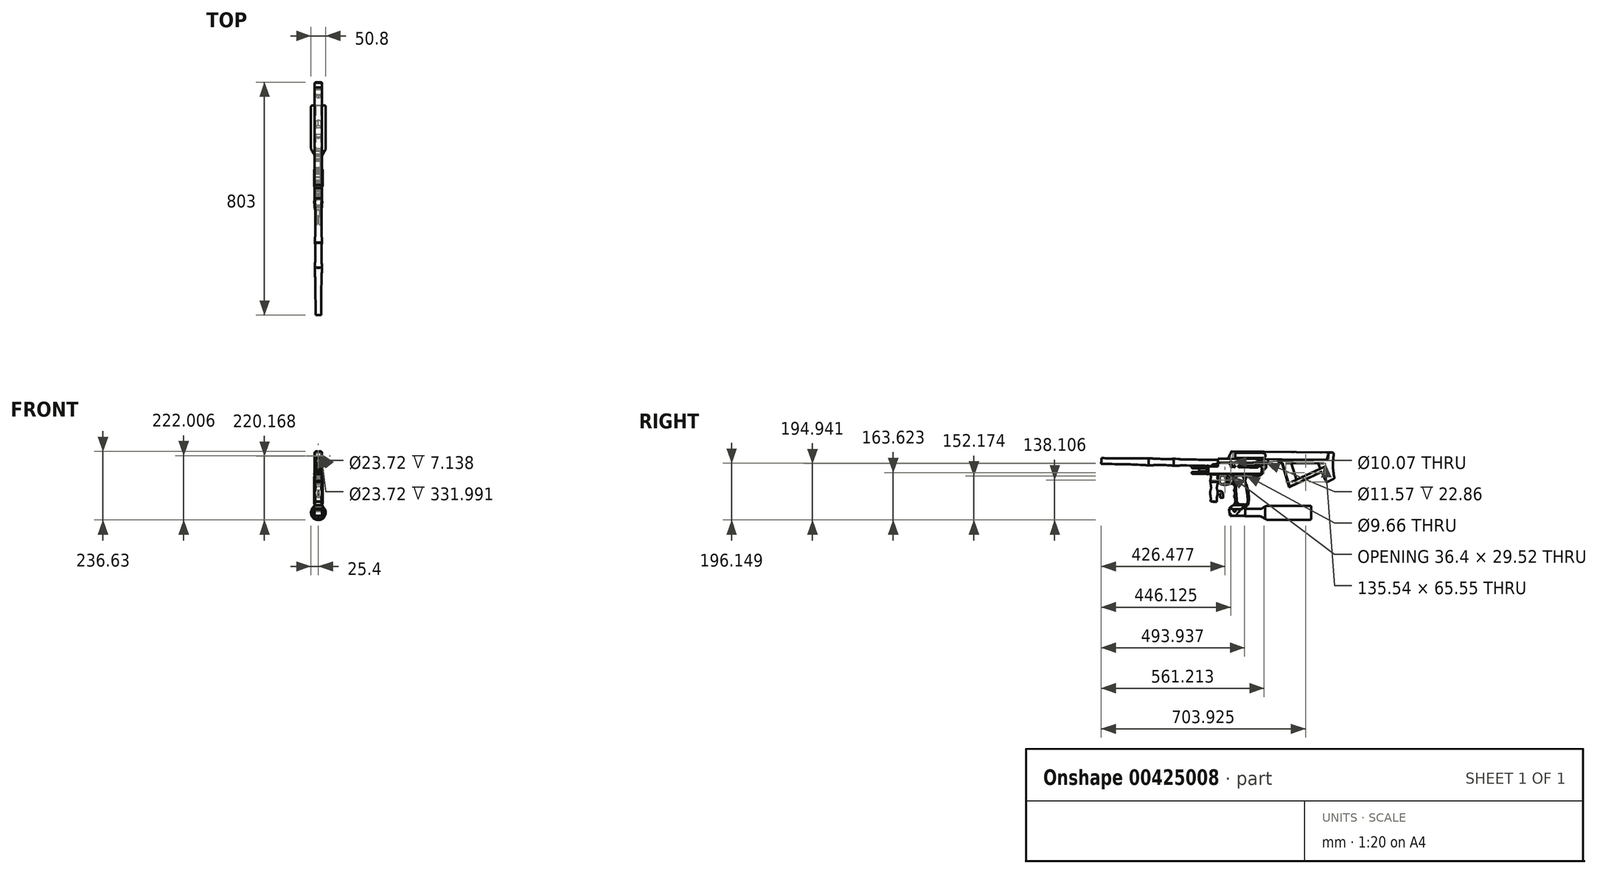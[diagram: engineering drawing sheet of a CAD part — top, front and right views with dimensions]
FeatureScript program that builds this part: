
annotation { "Feature Type Name" : "Feature", "Feature Type Description" : "" }
export const myFeature = defineFeature(function(context is Context, id is Id, definition is map)
    precondition{}
    {
        {
            var Q0;
            Q0=qCreatedBy(makeId("Right.planeOp"),FACE);
            var sketch = newSketch(context, id + "F0", { "sketchPlane" : qUnion([Q0])});
            skLineSegment(sketch, "E0", {"start": v(0, 12.7) * mm, "end": v(55.88, 12.7) * mm});
            skLineSegment(sketch, "E1", {"start": v(55.88, 12.7) * mm, "end": v(76.2, 25.4) * mm});
            skLineSegment(sketch, "E2", {"start": v(76.2, 25.4) * mm, "end": v(228.6, 25.4) * mm});
            skLineSegment(sketch, "E3", {"start": v(228.6, 25.4) * mm, "end": v(228.6, 0) * mm});
            skLineSegment(sketch, "E4", {"start": v(0, 12.7) * mm, "end": v(0, 0) * mm});
            skLineSegment(sketch, "E5", {"start": v(0, 0) * mm, "end": v(228.6, 0) * mm});
            skLineSegment(sketch, "E6", {"start": v(38.1, 12.7) * mm, "end": v(38.1, 0) * mm, "construction": true});
            skSolve(sketch);
        }
        {
            var Q0;
            Q0=makeQuery(id+"F0.imprint","IMPRINT",FACE,{"disambiguationData":[TD([[makeQuery(id+"F0.imprint","IMPRINT",EDGE,{"derivedFrom":sQuery(id+"F0.wireOp",EDGE,"E0")}),-1.0]])]});
            var Q1;
            Q1=sQuery(id+"F0.wireOp",EDGE,"E5");
            revolve(context, id + "F1", {"entities" : qUnion([Q0]), "axis" : qUnion([Q1]), "revolveType" : RevolveType.FULL});
        }
        {
            var Q0;
            Q0=makeQuery(id+"F1.opRevolve","SWEPT_EDGE",EDGE,{"disambiguationData":[OSD([sQuery(id+"F0.wireOp",EDGE,"E0"),sQuery(id+"F0.wireOp",EDGE,"E1")])]});
            fillet(context, id + "F2", {"entities" : qUnion([Q0]), "radius" : 12.7 * mm, "tangentPropagation" : true, "allowEdgeOverflow" : false});
        }
        {
            var Q0;
            Q0=makeQuery(id+"F1.opRevolve","SWEPT_EDGE",EDGE,{"disambiguationData":[OSD([sQuery(id+"F0.wireOp",EDGE,"E1"),sQuery(id+"F0.wireOp",EDGE,"E2")])]});
            fillet(context, id + "F3", {"entities" : qUnion([Q0]), "radius" : 25.4 * mm, "tangentPropagation" : true, "allowEdgeOverflow" : false});
        }
        {
            var Q0;
            Q0=makeQuery(id+"F1.opRevolve","SWEPT_EDGE",EDGE,{"disambiguationData":[OSD([sQuery(id+"F0.wireOp",EDGE,"E2"),sQuery(id+"F0.wireOp",EDGE,"E3")])]});
            fillet(context, id + "F4", {"entities" : qUnion([Q0]), "radius" : 5.08 * mm, "tangentPropagation" : true, "allowEdgeOverflow" : false});
        }
        {
            var Q0;
            Q0=qCreatedBy(makeId("Right.planeOp"),FACE);
            var sketch = newSketch(context, id + "F5", { "sketchPlane" : qUnion([Q0])});
            skLineSegment(sketch, "E7", {"start": v(-34.8, 25.58) * mm, "end": v(8.85, 25.58) * mm});
            skArc(sketch, "E8", {"start": v(8.85, 25.58) * mm, "mid": v(11.47, 26.54) * mm, "end": v(12.84, 28.97) * mm});
            skArc(sketch, "E9", {"start": v(12.84, 28.97) * mm, "mid": v(13.6, 66.51) * mm, "end": v(3.93, 102.8) * mm});
            skArc(sketch, "E10", {"start": v(20.6, 127.96) * mm, "mid": v(5.51, 119.85) * mm, "end": v(3.93, 102.8) * mm});
            skLineSegment(sketch, "E11", {"start": v(20.6, 127.96) * mm, "end": v(51.69, 127.96) * mm});
            skLineSegment(sketch, "E12", {"start": v(36.38, 133.85) * mm, "end": v(57.22, 133.85) * mm});
            skLineSegment(sketch, "E13", {"start": v(57.22, 133.85) * mm, "end": v(57.22, 130.34) * mm});
            skLineSegment(sketch, "E14", {"start": v(57.22, 130.34) * mm, "end": v(51.69, 127.96) * mm});
            skLineSegment(sketch, "E15", {"start": v(36.38, 133.85) * mm, "end": v(-87.79, 133.99) * mm});
            skLineSegment(sketch, "E16", {"start": v(-87.79, 133.99) * mm, "end": v(-87.82, 103.6) * mm});
            skArc(sketch, "E17", {"start": v(-87.82, 103.6) * mm, "mid": v(-86.98, 100.92) * mm, "end": v(-84.74, 99.2) * mm});
            skArc(sketch, "E18", {"start": v(-84.74, 99.2) * mm, "mid": v(-67.88, 96.22) * mm, "end": v(-51.03, 99.2) * mm});
            skArc(sketch, "E19", {"start": v(-35.1, 80.6) * mm, "mid": v(-36.61, 95.42) * mm, "end": v(-51.03, 99.2) * mm});
            skLineSegment(sketch, "E20", {"start": v(36.38, 133.85) * mm, "end": v(36.38, 127.96) * mm});
            skLineSegment(sketch, "E21", {"start": v(-35.1, 80.6) * mm, "end": v(-37.34, 76.5) * mm});
            skArc(sketch, "E22", {"start": v(-37.34, 55.45) * mm, "mid": v(-33.29, 65.98) * mm, "end": v(-37.34, 76.5) * mm});
            skArc(sketch, "E23", {"start": v(-34.39, 32.06) * mm, "mid": v(-31.83, 44.26) * mm, "end": v(-37.34, 55.45) * mm});
            skArc(sketch, "E24", {"start": v(-34.39, 32.06) * mm, "mid": v(-35.38, 28.87) * mm, "end": v(-34.8, 25.58) * mm});
            skFitSpline(sketch, "E25", {"points": [v(-85.65, 112.62) * mm, v(-85.36, 121.7) * mm, v(-85, 123.52) * mm, v(-84.11, 124.91) * mm, v(-82.58, 126.23) * mm, v(-80.53, 127.18) * mm, v(-62.02, 127.4) * mm, v(-58.15, 126.45) * mm, v(-54.42, 124.76) * mm, v(-51.56, 121.91) * mm, v(-49.59, 117.45) * mm, v(-49.22, 112.55) * mm, v(-50.17, 106.4) * mm, v(-52.15, 102.6) * mm, v(-55.59, 99.97) * mm, v(-59.83, 98.43) * mm, v(-70.87, 98.07) * mm, v(-81.63, 99.9) * mm, v(-84.7, 102.16) * mm, v(-85.72, 105.23) * mm, v(-85.65, 112.62) * mm]});
            skArc(sketch, "E26", {"start": v(-26.53, 127.42) * mm, "mid": v(-29.86, 126.09) * mm, "end": v(-31.18, 122.76) * mm});
            skArc(sketch, "E27", {"start": v(-4.85, 122.48) * mm, "mid": v(-7.37, 125.75) * mm, "end": v(-11.28, 127.05) * mm});
            skArc(sketch, "E28", {"start": v(10.82, 32.35) * mm, "mid": v(7.26, 78.16) * mm, "end": v(-4.85, 122.48) * mm});
            skArc(sketch, "E29", {"start": v(5.99, 27.7) * mm, "mid": v(9.37, 29.02) * mm, "end": v(10.82, 32.35) * mm});
            skArc(sketch, "E30", {"start": v(-26.4, 32.85) * mm, "mid": v(-24.9, 29.7) * mm, "end": v(-21.66, 28.36) * mm});
            skArc(sketch, "E31", {"start": v(-31.18, 122.76) * mm, "mid": v(-29.39, 77.77) * mm, "end": v(-26.4, 32.85) * mm});
            skLineSegment(sketch, "E32", {"start": v(-26.53, 127.42) * mm, "end": v(-11.28, 127.05) * mm});
            skLineSegment(sketch, "E33", {"start": v(-21.66, 28.36) * mm, "end": v(5.99, 27.7) * mm});
            skFitSpline(sketch, "E34", {"points": [v(-42.23, 99.25) * mm, v(-39.9, 104.21) * mm, v(-38.86, 113.42) * mm, v(-40.72, 121.38) * mm, v(-45.27, 128.83) * mm, v(-50.65, 133.95) * mm], "startDerivative": vector(15.33, 26.3) * mm, "endDerivative": vector(-28.38, 23.96) * mm});
            skLineSegment(sketch, "E35", {"start": v(-50.31, 105.95) * mm, "end": v(-59.35, 105.95) * mm});
            skLineSegment(sketch, "E36", {"start": v(-62.76, 127.47) * mm, "end": v(-63.34, 125.85) * mm});
            skLineSegment(sketch, "E37", {"start": v(-63.34, 125.85) * mm, "end": v(-66.8, 123.46) * mm});
            skLineSegment(sketch, "E38", {"start": v(-66.8, 123.46) * mm, "end": v(-66.8, 121.65) * mm});
            skArc(sketch, "E39", {"start": v(-59.35, 105.95) * mm, "mid": v(-59, 116.44) * mm, "end": v(-66.8, 123.46) * mm});
            skArc(sketch, "E40", {"start": v(-68.63, 101.75) * mm, "mid": v(-64.25, 110.54) * mm, "end": v(-68.14, 119.55) * mm});
            skArc(sketch, "E41", {"start": v(-68.63, 101.75) * mm, "mid": v(-68.81, 100.98) * mm, "end": v(-68.11, 100.6) * mm});
            skArc(sketch, "E42", {"start": v(-68.11, 100.6) * mm, "mid": v(-63.21, 102.43) * mm, "end": v(-59.35, 105.95) * mm});
            skLineSegment(sketch, "E43", {"start": v(-68.14, 119.55) * mm, "end": v(-66.8, 121.65) * mm});
            skLineSegment(sketch, "E44", {"start": v(-119.06, 133.99) * mm, "end": v(-90.1, 133.99) * mm});
            skLineSegment(sketch, "E45", {"start": v(-116.98, 37.9) * mm, "end": v(-95.76, 37.9) * mm});
            skLineSegment(sketch, "E46", {"start": v(-104.57, 133.99) * mm, "end": v(-106.37, 37.9) * mm});
            skFitSpline(sketch, "E47", {"points": [v(-95.76, 37.9) * mm, v(-95.76, 41) * mm, v(-95.76, 50.82) * mm, v(-94.35, 58.22) * mm, v(-93.32, 64.11) * mm, v(-93.53, 75.08) * mm, v(-94.77, 80.46) * mm, v(-95.76, 85.73) * mm, v(-94.54, 92.26) * mm, v(-93.18, 100.75) * mm, v(-92.32, 106.04) * mm, v(-92.07, 109.62) * mm, v(-92.32, 114.77) * mm, v(-93.8, 119.44) * mm, v(-93.43, 123.75) * mm, v(-92.2, 129.29) * mm, v(-90.1, 133.99) * mm], "startDerivative": vector(1.1, 57.96) * mm, "endDerivative": vector(36.56, 91.45) * mm});
            skLineSegment(sketch, "E48", {"start": v(-105.1, 105.63) * mm, "end": v(-92.41, 105.4) * mm});
            skLineSegment(sketch, "E49", {"start": v(-105.03, 109.62) * mm, "end": v(-92.07, 109.62) * mm});
            skLineSegment(sketch, "E50", {"start": v(-90.1, 133.99) * mm, "end": v(-87.79, 133.99) * mm});
            skLineSegment(sketch, "E51", {"start": v(-87.79, 133.99) * mm, "end": v(-87.79, 133.99) * mm});
            skLineSegment(sketch, "E52", {"start": v(-119.06, 133.99) * mm, "end": v(-119.88, 136.58) * mm, "construction": true});
            skLineSegment(sketch, "E53", {"start": v(-119.88, 136.58) * mm, "end": v(-124.7, 136.58) * mm, "construction": true});
            skLineSegment(sketch, "E54", {"start": v(-124.7, 136.58) * mm, "end": v(-124.7, 159) * mm});
            skLineSegment(sketch, "E55", {"start": v(-124.7, 159) * mm, "end": v(-91.58, 159) * mm});
            skLineSegment(sketch, "E56", {"start": v(-91.58, 159) * mm, "end": v(-91.58, 186.35) * mm});
            skLineSegment(sketch, "E57", {"start": v(-91.58, 186.35) * mm, "end": v(58.12, 184.65) * mm});
            skLineSegment(sketch, "E58", {"start": v(58.12, 184.65) * mm, "end": v(80.35, 183.9) * mm});
            skFitSpline(sketch, "E59", {"points": [v(80.35, 183.9) * mm, v(80.35, 175.9) * mm, v(79.82, 173.8) * mm, v(77.49, 172.2) * mm, v(76.32, 170.65) * mm, v(74.97, 167.4) * mm, v(74.47, 162.84) * mm, v(74.1, 156.94) * mm, v(72.88, 153.08) * mm, v(70.84, 151.59) * mm, v(66.54, 147.1) * mm, v(62.97, 139.71) * mm, v(61.31, 134.42) * mm, v(61.08, 133.83) * mm, v(60.68, 133.46) * mm, v(57.22, 133.33) * mm], "startDerivative": vector(0.59, -95.8) * mm, "endDerivative": vector(-85.27, 1.37) * mm});
            skFitSpline(sketch, "E60", {"points": [v(58.12, 184.65) * mm, v(58.12, 180.63) * mm, v(57.78, 178.99) * mm, v(56.76, 178.55) * mm, v(42.34, 175.33) * mm, v(39.81, 174.2) * mm, v(39.03, 173.58) * mm, v(38.25, 172.1) * mm, v(37.88, 168.45) * mm, v(38.25, 166.07) * mm, v(39.97, 164.06) * mm, v(44.25, 162.64) * mm, v(50.45, 161.47) * mm, v(55.52, 159.55) * mm, v(58.12, 157.64) * mm, v(58.98, 156.2) * mm, v(58.37, 133.3) * mm], "startDerivative": vector(0, -170.26) * mm, "endDerivative": vector(-0.04, -213.8) * mm});
            skFitSpline(sketch, "E61", {"points": [v(59.43, 176.27) * mm, v(46.5, 174.05) * mm, v(43.35, 173.42) * mm, v(41.9, 172.4) * mm, v(40.6, 170.58) * mm, v(40.6, 168.87) * mm, v(41.02, 167.01) * mm, v(42.37, 166.03) * mm, v(51.37, 163.75) * mm, v(55.97, 162.46) * mm, v(59.95, 162.51) * mm, v(60.68, 163.8) * mm, v(61.2, 165.61) * mm, v(59.8, 167.94) * mm, v(59.43, 170.22) * mm, v(60.16, 171.98) * mm, v(60.83, 173.73) * mm, v(60.57, 175.34) * mm, v(59.43, 176.27) * mm]});
            skCircle(sketch, "E62", {"center": v(67.35, 169.54) * mm, "radius": 5.78 * mm});
            skCircle(sketch, "E63", {"center": v(0.08, 126.77) * mm, "radius": 4.83 * mm});
            skCircle(sketch, "E64", {"center": v(-47.74, 170.75) * mm, "radius": 5.03 * mm});
            skLineSegment(sketch, "E65", {"start": v(-91.58, 182.73) * mm, "end": v(-91.58, 159.18) * mm});
            skLineSegment(sketch, "E66", {"start": v(-493.5, 187.98) * mm, "end": v(-493.5, 168.75) * mm});
            skLineSegment(sketch, "E67", {"start": v(-493.5, 178.36) * mm, "end": v(-91.58, 170.96) * mm});
            skFitSpline(sketch, "E68", {"points": [v(-91.58, 182.73) * mm, v(-119.26, 182.73) * mm, v(-132.58, 182.45) * mm, v(-141.54, 182.4) * mm, v(-218.62, 183.74) * mm, v(-221.32, 183.89) * mm, v(-223.33, 184.44) * mm, v(-225.09, 184.99) * mm, v(-228.56, 185.2) * mm, v(-244.1, 185.57) * mm, v(-247.38, 185.61) * mm, v(-248.94, 185.26) * mm, v(-250.38, 184.74) * mm, v(-253.38, 184.48) * mm, v(-258.12, 184.52) * mm, v(-306.46, 185.9) * mm, v(-318.87, 186.83) * mm, v(-329.63, 187.14) * mm, v(-343.7, 187.27) * mm, v(-381.34, 186.78) * mm, v(-423.66, 187.15) * mm, v(-493.5, 187.98) * mm], "startDerivative": vector(-460.1, 2.23) * mm, "endDerivative": vector(-701.67, 7.48) * mm});
            skLineSegment(sketch, "E69", {"start": v(-330.43, 175.36) * mm, "end": v(-330.21, 187.15) * mm});
            skLineSegment(sketch, "E70", {"start": v(-244.33, 173.77) * mm, "end": v(-244.1, 185.57) * mm});
            skFitSpline(sketch, "E71", {"points": [v(4.95, 25.58) * mm, v(5.8, 23.6) * mm, v(5.17, 21.07) * mm, v(3.34, 19.04) * mm, v(1.12, 19.26) * mm, v(-6.59, 18.86) * mm, v(-8.65, 17.1) * mm, v(-8.31, 15.51) * mm, v(-8.57, 12.67) * mm, v(-8.87, 12.04) * mm, v(-51.36, 12.84) * mm, v(-51.75, 12.98) * mm, v(-51.8, 17.75) * mm, v(-51.48, 18.04) * mm, v(-42.1, 23.94) * mm, v(-40.14, 25.32) * mm, v(-34.8, 25.58) * mm], "startDerivative": vector(22.9, -41.19) * mm, "endDerivative": vector(123.88, 5.53) * mm});
            skLineSegment(sketch, "E72", {"start": v(-49.82, 12.84) * mm, "end": v(-54.66, 10.86) * mm});
            skLineSegment(sketch, "E73", {"start": v(-54.66, 10.86) * mm, "end": v(-50.05, -10.71) * mm});
            skLineSegment(sketch, "E74", {"start": v(-50.05, -10.71) * mm, "end": v(1.1, -10.71) * mm});
            skLineSegment(sketch, "E75", {"start": v(1.1, -10.71) * mm, "end": v(1.1, 15.65) * mm});
            skLineSegment(sketch, "E76", {"start": v(1.1, 15.65) * mm, "end": v(-8.31, 15.51) * mm});
            skFitSpline(sketch, "E77", {"points": [v(-29.52, -10.71) * mm, v(-28.92, -8.02) * mm, v(-27.7, -5.93) * mm, v(-24.57, -1.75) * mm, v(-21.09, 1.81) * mm, v(-18.48, 4.86) * mm, v(-18.13, 7.12) * mm, v(-18.83, 9.56) * mm, v(-21.43, 11.86) * mm], "startDerivative": vector(4.19, 25.46) * mm, "endDerivative": vector(-24.07, 17.07) * mm});
            skCircle(sketch, "E78", {"center": v(-34.92, 7.3) * mm, "radius": 3.9 * mm});
            skLineSegment(sketch, "E79", {"start": v(-44.21, 159.76) * mm, "end": v(-35.63, 159.76) * mm});
            skLineSegment(sketch, "E80", {"start": v(-18.9, 159.55) * mm, "end": v(43.85, 158.68) * mm});
            skArc(sketch, "E81.0.startCap", {"start": v(-44.21, 158.5) * mm, "mid": v(-45.48, 159.76) * mm, "end": v(-44.21, 161.03) * mm});
            skArc(sketch, "E81.0.endCap", {"start": v(-35.63, 161.03) * mm, "mid": v(-34.36, 159.76) * mm, "end": v(-35.63, 158.5) * mm});
            skLineSegment(sketch, "E81.0.left", {"start": v(-44.21, 161.03) * mm, "end": v(-35.63, 161.03) * mm});
            skLineSegment(sketch, "E81.0.right", {"start": v(-44.21, 158.5) * mm, "end": v(-35.63, 158.5) * mm});
            skArc(sketch, "E81.1.startCap", {"start": v(-18.93, 158.28) * mm, "mid": v(-20.18, 159.57) * mm, "end": v(-18.9, 160.82) * mm});
            skArc(sketch, "E81.1.endCap", {"start": v(43.87, 159.95) * mm, "mid": v(45.12, 158.66) * mm, "end": v(43.83, 157.4) * mm});
            skLineSegment(sketch, "E81.1.left", {"start": v(-18.9, 160.82) * mm, "end": v(43.87, 159.95) * mm});
            skLineSegment(sketch, "E81.1.right", {"start": v(-18.93, 158.28) * mm, "end": v(43.83, 157.4) * mm});
            skLineSegment(sketch, "E82", {"start": v(-124.7, 159) * mm, "end": v(-124.7, 162.28) * mm});
            skLineSegment(sketch, "E83", {"start": v(-124.7, 162.28) * mm, "end": v(-130.05, 162.28) * mm});
            skLineSegment(sketch, "E84", {"start": v(-130.05, 162.28) * mm, "end": v(-130.05, 132.7) * mm});
            skLineSegment(sketch, "E85", {"start": v(-130.05, 132.7) * mm, "end": v(-124.7, 132.7) * mm});
            skLineSegment(sketch, "E86", {"start": v(-124.7, 132.7) * mm, "end": v(-124.7, 136.58) * mm});
            skLineSegment(sketch, "E87", {"start": v(-130.05, 162.28) * mm, "end": v(-201.74, 162.28) * mm});
            skLineSegment(sketch, "E88", {"start": v(-201.74, 162.28) * mm, "end": v(-201.74, 156.74) * mm});
            skLineSegment(sketch, "E89", {"start": v(-201.74, 156.74) * mm, "end": v(-130.05, 156.74) * mm});
            skLineSegment(sketch, "E90", {"start": v(-55.46, 186.85) * mm, "end": v(-33.3, 186.6) * mm});
            skLineSegment(sketch, "E91", {"start": v(-44.39, 186.72) * mm, "end": v(-44.49, 177.92) * mm});
            skLineSegment(sketch, "E92", {"start": v(-119.06, 133.99) * mm, "end": v(-124.7, 133.99) * mm});
            skLineSegment(sketch, "E93", {"start": v(-93.4, 74.02) * mm, "end": v(-83.18, 74.02) * mm});
            skLineSegment(sketch, "E94", {"start": v(-93.4, 63.3) * mm, "end": v(-84.59, 63.3) * mm});
            skLineSegment(sketch, "E95", {"start": v(-84.59, 63.3) * mm, "end": v(-84.59, 51.13) * mm});
            skLineSegment(sketch, "E96", {"start": v(-84.59, 51.13) * mm, "end": v(-74.65, 51.13) * mm});
            skLineSegment(sketch, "E97", {"start": v(-74.65, 51.13) * mm, "end": v(-74.65, 65.49) * mm});
            skArc(sketch, "E98", {"start": v(-74.65, 65.49) * mm, "mid": v(-77.15, 71.52) * mm, "end": v(-83.18, 74.02) * mm});
            skLineSegment(sketch, "E99.0", {"start": v(-79.48, 51.13) * mm, "end": v(-79.48, 65.49) * mm});
            skArc(sketch, "E99.1", {"start": v(-79.48, 65.49) * mm, "mid": v(-80.56, 68.1) * mm, "end": v(-83.18, 69.19) * mm});
            skLineSegment(sketch, "E99.2", {"start": v(-93.4, 69.19) * mm, "end": v(-83.18, 69.19) * mm});
            skSolve(sketch);
        }
        {
            var Q0;
            {var subQ17=sQuery(id+"F5.wireOp",EDGE,"E12");Q0=makeQuery(id+"F5.imprint","IMPRINT",FACE,{"disambiguationData":[TD([[makeQuery(id+"F5.imprint","IMPRINT",EDGE,{"derivedFrom":subQ17}),1.0]])]});}
            var Q1;
            {var subQ3=sQuery(id+"F5.wireOp",EDGE,"E72");Q1=makeQuery(id+"F5.imprint","IMPRINT",FACE,{"disambiguationData":[TD([[makeQuery(id+"F5.imprint","IMPRINT",EDGE,{"derivedFrom":subQ3}),1.0]])]});}
            extrude(context, id + "F6", {"entities" : qUnion([Q0, Q1]), "operationType" : NewBodyOperationType.ADD, "depth" : 25.4 * mm, "offsetDistance" : 25.4 * mm, "symmetric" : true});
        }
        {
            var Q0;
            {var subQ2=sQuery(id+"F5.wireOp",EDGE,"E8");Q0=makeQuery(id+"F5.imprint","IMPRINT",FACE,{"disambiguationData":[TD([[makeQuery(id+"F5.imprint","IMPRINT",EDGE,{"derivedFrom":subQ2}),1.0]])]});}
            var Q1;
            {var subQ1=sQuery(id+"F5.wireOp",EDGE,"E75");Q1=makeQuery(id+"F5.imprint","IMPRINT",FACE,{"disambiguationData":[TD([[makeQuery(id+"F5.imprint","IMPRINT",EDGE,{"derivedFrom":subQ1}),1.0]])]});}
            var Q2;
            Q2=makeQuery(id+"F5.imprint","IMPRINT",FACE,{"disambiguationData":[TD([[makeQuery(id+"F5.imprint","IMPRINT",EDGE,{"derivedFrom":sQuery(id+"F5.wireOp",EDGE,"E78")}),1.0]])]});
            var Q3;
            Q3=makeQuery(id+"F5.imprint","IMPRINT",FACE,{"disambiguationData":[TD([[makeQuery(id+"F5.imprint","IMPRINT",EDGE,{"derivedFrom":sQuery(id+"F5.wireOp",EDGE,"E64")}),1.0]])]});
            var Q4;
            Q4=makeQuery(id+"F5.imprint","IMPRINT",FACE,{"disambiguationData":[TD([[makeQuery(id+"F5.imprint","IMPRINT",EDGE,{"derivedFrom":sQuery(id+"F5.wireOp",EDGE,"E62")}),1.0]])]});
            extrude(context, id + "F7", {"entities" : qUnion([Q0, Q1, Q2, Q3, Q4]), "depth" : 22.86 * mm, "offsetDistance" : 25.4 * mm, "symmetric" : true});
        }
        {
            var Q0;
            Q0=makeQuery(id+"F5.imprint","IMPRINT",FACE,{"disambiguationData":[TD([[makeQuery(id+"F5.imprint","IMPRINT",EDGE,{"derivedFrom":sQuery(id+"F5.wireOp",EDGE,"E26")}),1.0]])]});
            var Q1;
            {var subQ0=sQuery(id+"F5.wireOp",EDGE,"E71");var subQ4=sQuery(id+"F5.wireOp",EDGE,"E7");var subQ5=makeQuery(id+"F5.imprint","INTERSECT",VERTEX,{"derivedFrom":[subQ4,subQ0]});Q1=makeQuery(id+"F5.imprint","IMPRINT",FACE,{"disambiguationData":[TD([[makeQuery(id+"F5.imprint","IMPRINT",EDGE,{"disambiguationData":[TD([[subQ5,-1.0]])],"derivedFrom":subQ0}),-1.0]])]});}
            extrude(context, id + "F8", {"entities" : qUnion([Q0, Q1]), "depth" : 29.2 * mm, "offsetDistance" : 25.4 * mm, "symmetric" : true});
        }
        {
            var Q0;
            {var subQ1=sQuery(id+"F5.wireOp",EDGE,"E16");Q0=makeQuery(id+"F5.imprint","IMPRINT",FACE,{"disambiguationData":[TD([[makeQuery(id+"F5.imprint","IMPRINT",EDGE,{"derivedFrom":subQ1}),1.0]])]});}
            var Q1;
            Q1=makeQuery(id+"F5.imprint","IMPRINT",FACE,{"disambiguationData":[TD([[makeQuery(id+"F5.imprint","IMPRINT",EDGE,{"derivedFrom":sQuery(id+"F5.wireOp",EDGE,"E63")}),1.0]])]});
            extrude(context, id + "F9", {"entities" : qUnion([Q0, Q1]), "depth" : 12.7 * mm, "offsetDistance" : 25.4 * mm, "symmetric" : true});
        }
        {
            var Q0;
            Q0=makeQuery(id+"F5.imprint","IMPRINT",FACE,{"disambiguationData":[TD([[makeQuery(id+"F5.imprint","IMPRINT",EDGE,{"derivedFrom":sQuery(id+"F5.wireOp",EDGE,"E38")}),1.0]])]});
            extrude(context, id + "F10", {"entities" : qUnion([Q0]), "depth" : 6.35 * mm, "offsetDistance" : 25.4 * mm, "symmetric" : true});
        }
        {
            var Q0;
            {var subQ1=sQuery(id+"F5.wireOp",EDGE,"E35");Q0=makeQuery(id+"F5.imprint","IMPRINT",FACE,{"disambiguationData":[TD([[makeQuery(id+"F5.imprint","IMPRINT",EDGE,{"derivedFrom":subQ1}),-1.0]])]});}
            extrude(context, id + "F11", {"entities" : qUnion([Q0]), "depth" : 3.8 * mm, "offsetDistance" : 25.4 * mm, "symmetric" : true});
        }
        {
            var Q0;
            {var subQ3=sQuery(id+"F5.wireOp",EDGE,"E12");Q0=makeQuery(id+"F5.imprint","IMPRINT",FACE,{"disambiguationData":[TD([[makeQuery(id+"F5.imprint","IMPRINT",EDGE,{"derivedFrom":subQ3}),-1.0]])]});}
            var Q1;
            {var subQ2=sQuery(id+"F5.wireOp",EDGE,"E58");Q1=makeQuery(id+"F5.imprint","IMPRINT",FACE,{"disambiguationData":[TD([[makeQuery(id+"F5.imprint","IMPRINT",EDGE,{"derivedFrom":subQ2}),-1.0]])]});}
            var Q2;
            Q2=makeQuery(id+"F5.imprint","IMPRINT",FACE,{"disambiguationData":[TD([[makeQuery(id+"F5.imprint","IMPRINT",EDGE,{"derivedFrom":sQuery(id+"F5.wireOp",EDGE,"E54")}),1.0]])]});
            extrude(context, id + "F12", {"entities" : qUnion([Q0, Q1, Q2]), "depth" : 22.86 * mm, "offsetDistance" : 25.4 * mm, "symmetric" : true});
        }
        {
            var Q0;
            {var subQ5=sQuery(id+"F5.wireOp",EDGE,"E49");Q0=makeQuery(id+"F5.imprint","IMPRINT",FACE,{"disambiguationData":[TD([[makeQuery(id+"F5.imprint","IMPRINT",EDGE,{"derivedFrom":subQ5}),1.0]])]});}
            var Q1;
            {var subQ5=sQuery(id+"F5.wireOp",EDGE,"E48");Q1=makeQuery(id+"F5.imprint","IMPRINT",FACE,{"disambiguationData":[TD([[makeQuery(id+"F5.imprint","IMPRINT",EDGE,{"derivedFrom":subQ5}),-1.0]])]});}
            var Q2;
            Q2=sQuery(id+"F5.wireOp",EDGE,"E46");
            revolve(context, id + "F13", {"entities" : qUnion([Q0, Q1]), "axis" : qUnion([Q2]), "revolveType" : RevolveType.FULL});
        }
        {
            var Q0;
            {var subQ0=sQuery(id+"F5.wireOp",EDGE,"E48");Q0=makeQuery(id+"F5.imprint","IMPRINT",FACE,{"disambiguationData":[TD([[makeQuery(id+"F5.imprint","IMPRINT",EDGE,{"derivedFrom":subQ0}),1.0]])]});}
            var Q1;
            Q1=sQuery(id+"F5.wireOp",EDGE,"E46");
            revolve(context, id + "F14", {"entities" : qUnion([Q0]), "axis" : qUnion([Q1]), "revolveType" : RevolveType.FULL});
        }
        {
            var Q0;
            {var subQ5=sQuery(id+"F5.wireOp",EDGE,"E70");Q0=makeQuery(id+"F5.imprint","IMPRINT",FACE,{"disambiguationData":[TD([[makeQuery(id+"F5.imprint","IMPRINT",EDGE,{"derivedFrom":subQ5}),-1.0]])]});}
            var Q1;
            {var subQ5=sQuery(id+"F5.wireOp",EDGE,"E69");Q1=makeQuery(id+"F5.imprint","IMPRINT",FACE,{"disambiguationData":[TD([[makeQuery(id+"F5.imprint","IMPRINT",EDGE,{"derivedFrom":subQ5}),1.0]])]});}
            var Q2;
            Q2=sQuery(id+"F5.wireOp",EDGE,"E67");
            revolve(context, id + "F15", {"entities" : qUnion([Q0, Q1]), "axis" : qUnion([Q2]), "revolveType" : RevolveType.FULL});
        }
        {
            var Q0;
            {var subQ0=sQuery(id+"F5.wireOp",EDGE,"E69");Q0=makeQuery(id+"F5.imprint","IMPRINT",FACE,{"disambiguationData":[TD([[makeQuery(id+"F5.imprint","IMPRINT",EDGE,{"derivedFrom":subQ0}),-1.0]])]});}
            var Q1;
            Q1=sQuery(id+"F5.wireOp",EDGE,"E67");
            revolve(context, id + "F16", {"entities" : qUnion([Q0]), "axis" : qUnion([Q1]), "revolveType" : RevolveType.FULL});
        }
        {
            var Q0;
            Q0=makeQuery(id+"F6.opExtrude","CAP_EDGE",EDGE,{"disambiguationData":[OSD([sQuery(id+"F5.wireOp",EDGE,"E57")])],"isStart":false});
            var Q1;
            Q1=makeQuery(id+"F6.opExtrude","CAP_EDGE",EDGE,{"disambiguationData":[OSD([sQuery(id+"F5.wireOp",EDGE,"E57")])],"isStart":true});
            var Q2;
            Q2=makeQuery(id+"F12.opExtrude","CAP_EDGE",EDGE,{"disambiguationData":[OSD([sQuery(id+"F5.wireOp",EDGE,"E58")])],"isStart":false});
            var Q3;
            Q3=makeQuery(id+"F12.opExtrude","CAP_EDGE",EDGE,{"disambiguationData":[OSD([sQuery(id+"F5.wireOp",EDGE,"E58")])],"isStart":true});
            fillet(context, id + "F17", {"entities" : qUnion([Q0, Q1, Q2, Q3]), "radius" : 10.16 * mm, "tangentPropagation" : true, "allowEdgeOverflow" : false});
        }
        {
            var Q0;
            Q0=qCreatedBy(makeId("Front.planeOp"),FACE);
            var sketch = newSketch(context, id + "F18", { "sketchPlane" : qUnion([Q0])});
            skLineSegment(sketch, "E100", {"start": v(0, 184.65) * mm, "end": v(0, 140.2) * mm});
            skFitSpline(sketch, "E101", {"points": [v(9.57, 133.3) * mm, v(11.05, 133.86) * mm, v(12.3, 138.16) * mm, v(12.14, 145.16) * mm, v(10.48, 151.24) * mm, v(7.41, 159.65) * mm, v(11.6, 168.5) * mm, v(13.15, 175.63) * mm, v(13.68, 184.33) * mm], "startDerivative": vector(38.05, 7.84) * mm, "endDerivative": vector(3.18, 60.22) * mm});
            skArc(sketch, "E102", {"start": v(9.57, 133.3) * mm, "mid": v(53.33, 155.46) * mm, "end": v(13.68, 184.33) * mm});
            skSolve(sketch);
        }
        {
            var Q0;
            Q0=makeQuery(id+"F18.imprint","IMPRINT",FACE,{"disambiguationData":[TD([[makeQuery(id+"F18.imprint","IMPRINT",EDGE,{"derivedFrom":sQuery(id+"F18.wireOp",EDGE,"E101")}),-1.0]])]});
            extrude(context, id + "F19", {"entities" : qUnion([Q0]), "operationType" : NewBodyOperationType.REMOVE, "oppositeDirection" : true, "depth" : 1322.83 * mm, "offsetDistance" : 25.4 * mm, "symmetric" : true});
        }
        {
            var Q0;
            Q0=makeQuery(id+"F8.opExtrude","CAP_FACE",FACE,{"disambiguationData":[OSD([sQuery(id+"F5.wireOp",EDGE,"E26"),sQuery(id+"F5.wireOp",EDGE,"E27"),sQuery(id+"F5.wireOp",EDGE,"E28"),sQuery(id+"F5.wireOp",EDGE,"E29"),sQuery(id+"F5.wireOp",EDGE,"E30"),sQuery(id+"F5.wireOp",EDGE,"E31"),sQuery(id+"F5.wireOp",EDGE,"E32"),sQuery(id+"F5.wireOp",EDGE,"E33")])],"isStart":false});
            var Q1;
            Q1=makeQuery(id+"F8.opExtrude","CAP_FACE",FACE,{"disambiguationData":[OSD([sQuery(id+"F5.wireOp",EDGE,"E26"),sQuery(id+"F5.wireOp",EDGE,"E27"),sQuery(id+"F5.wireOp",EDGE,"E28"),sQuery(id+"F5.wireOp",EDGE,"E29"),sQuery(id+"F5.wireOp",EDGE,"E30"),sQuery(id+"F5.wireOp",EDGE,"E31"),sQuery(id+"F5.wireOp",EDGE,"E32"),sQuery(id+"F5.wireOp",EDGE,"E33")])],"isStart":true});
            fillet(context, id + "F20", {"entities" : qUnion([Q0, Q1]), "radius" : 5.08 * mm, "tangentPropagation" : true, "allowEdgeOverflow" : false});
        }
        {
            var Q0;
            Q0=makeQuery(id+"F7.opExtrude","CAP_EDGE",EDGE,{"disambiguationData":[OSD([sQuery(id+"F5.wireOp",EDGE,"E34")])],"isStart":false});
            chamfer(context, id + "F21", {"entities" : qUnion([Q0]), "width" : 5.08 * mm, "tangentPropagation" : true});
        }
        {
            var Q0;
            Q0=makeQuery(id+"F7.opExtrude","CAP_EDGE",EDGE,{"disambiguationData":[OSD([sQuery(id+"F5.wireOp",EDGE,"E19")])],"isStart":false});
            var Q1;
            Q1=makeQuery(id+"F7.opExtrude","CAP_EDGE",EDGE,{"disambiguationData":[OSD([sQuery(id+"F5.wireOp",EDGE,"E21")])],"isStart":false});
            var Q2;
            Q2=makeQuery(id+"F7.opExtrude","CAP_EDGE",EDGE,{"disambiguationData":[OSD([sQuery(id+"F5.wireOp",EDGE,"E22")])],"isStart":false});
            var Q3;
            Q3=makeQuery(id+"F7.opExtrude","CAP_EDGE",EDGE,{"disambiguationData":[OSD([sQuery(id+"F5.wireOp",EDGE,"E23")])],"isStart":false});
            var Q4;
            Q4=makeQuery(id+"F7.opExtrude","CAP_EDGE",EDGE,{"disambiguationData":[OSD([sQuery(id+"F5.wireOp",EDGE,"E24")])],"isStart":false});
            var Q5;
            Q5=makeQuery(id+"F7.opExtrude","CAP_EDGE",EDGE,{"disambiguationData":[OSD([sQuery(id+"F5.wireOp",EDGE,"E9")])],"isStart":false});
            var Q6;
            Q6=makeQuery(id+"F7.opExtrude","CAP_EDGE",EDGE,{"disambiguationData":[OSD([sQuery(id+"F5.wireOp",EDGE,"E8")])],"isStart":false});
            var Q7;
            Q7=makeQuery(id+"F7.opExtrude","CAP_EDGE",EDGE,{"disambiguationData":[OSD([sQuery(id+"F5.wireOp",EDGE,"E10")])],"isStart":false});
            var Q8;
            Q8=makeQuery(id+"F7.opExtrude","CAP_EDGE",EDGE,{"disambiguationData":[OSD([sQuery(id+"F5.wireOp",EDGE,"E11")])],"isStart":false});
            var Q9;
            Q9=makeQuery(id+"F12.opExtrude","CAP_EDGE",EDGE,{"disambiguationData":[OSD([sQuery(id+"F5.wireOp",EDGE,"E11")])],"isStart":false});
            var Q10;
            Q10=makeQuery(id+"F7.opExtrude","CAP_EDGE",EDGE,{"disambiguationData":[OSD([sQuery(id+"F5.wireOp",EDGE,"E19")])],"isStart":true});
            var Q11;
            Q11=makeQuery(id+"F7.opExtrude","CAP_EDGE",EDGE,{"disambiguationData":[OSD([sQuery(id+"F5.wireOp",EDGE,"E21")])],"isStart":true});
            var Q12;
            Q12=makeQuery(id+"F7.opExtrude","CAP_EDGE",EDGE,{"disambiguationData":[OSD([sQuery(id+"F5.wireOp",EDGE,"E22")])],"isStart":true});
            var Q13;
            Q13=makeQuery(id+"F7.opExtrude","CAP_EDGE",EDGE,{"disambiguationData":[OSD([sQuery(id+"F5.wireOp",EDGE,"E23")])],"isStart":true});
            var Q14;
            Q14=makeQuery(id+"F7.opExtrude","CAP_EDGE",EDGE,{"disambiguationData":[OSD([sQuery(id+"F5.wireOp",EDGE,"E9")])],"isStart":true});
            var Q15;
            Q15=makeQuery(id+"F7.opExtrude","CAP_EDGE",EDGE,{"disambiguationData":[OSD([sQuery(id+"F5.wireOp",EDGE,"E8")])],"isStart":true});
            var Q16;
            Q16=makeQuery(id+"F12.opExtrude","CAP_EDGE",EDGE,{"disambiguationData":[OSD([sQuery(id+"F5.wireOp",EDGE,"E11")])],"isStart":true});
            var Q17;
            Q17=makeQuery(id+"F12.opExtrude","CAP_EDGE",EDGE,{"disambiguationData":[OSD([sQuery(id+"F5.wireOp",EDGE,"E14")])],"isStart":true});
            var Q18;
            Q18=makeQuery(id+"F12.opExtrude","CAP_EDGE",EDGE,{"disambiguationData":[OSD([sQuery(id+"F5.wireOp",EDGE,"E14")])],"isStart":false});
            fillet(context, id + "F22", {"entities" : qUnion([Q0, Q1, Q2, Q3, Q4, Q5, Q6, Q7, Q8, Q9, Q10, Q11, Q12, Q13, Q14, Q15, Q16, Q17, Q18]), "radius" : 2.54 * mm, "tangentPropagation" : true, "allowEdgeOverflow" : false});
        }
        {
            var Q0;
            Q0=makeQuery(id+"F19.boolean.opBoolean","INTERSECT",EDGE,{"derivedFrom":[makeQuery(id+"F6.opExtrude","SWEPT_FACE",FACE,{"disambiguationData":[OSD([sQuery(id+"F5.wireOp",EDGE,"E81.1.left")])]}),makeQuery(id+"F19.opExtrude","SWEPT_FACE",FACE,{"disambiguationData":[OSD([sQuery(id+"F18.wireOp",EDGE,"E101")])]})]});
            var Q1;
            Q1=makeQuery(id+"F19.boolean.opBoolean","INTERSECT",EDGE,{"derivedFrom":[makeQuery(id+"F6.opExtrude","SWEPT_FACE",FACE,{"disambiguationData":[OSD([sQuery(id+"F5.wireOp",EDGE,"E81.0.left")])]}),makeQuery(id+"F19.opExtrude","SWEPT_FACE",FACE,{"disambiguationData":[OSD([sQuery(id+"F18.wireOp",EDGE,"E101")])]})]});
            fillet(context, id + "F23", {"entities" : qUnion([Q0, Q1]), "radius" : 2.54 * mm, "tangentPropagation" : true, "allowEdgeOverflow" : false});
        }
        {
            var Q0;
            Q0=makeQuery(id+"F12.opExtrude","SWEPT_FACE",FACE,{"disambiguationData":[OSD([sQuery(id+"F5.wireOp",EDGE,"E84")])]});
            var sketch = newSketch(context, id + "F24", { "sketchPlane" : qUnion([Q0])});
            skCircle(sketch, "E103", {"center": v(5.52, 156.48) * mm, "radius": 2.97 * mm});
            skCircle(sketch, "E104", {"center": v(-6.53, 156.48) * mm, "radius": 2.97 * mm});
            skCircle(sketch, "E105", {"center": v(-0.52, 147.67) * mm, "radius": 5.1 * mm});
            skCircle(sketch, "E106", {"center": v(5.52, 137.24) * mm, "radius": 2.97 * mm});
            skCircle(sketch, "E107", {"center": v(-6.53, 137.24) * mm, "radius": 2.97 * mm});
            skSolve(sketch);
        }
        {
            var Q0;
            Q0 = qSketchRegion(id + "F24", true);
            extrude(context, id + "F25", {"entities" : qUnion([Q0]), "operationType" : NewBodyOperationType.ADD, "depth" : 52.32 * mm, "offsetDistance" : 25.4 * mm});
        }
        {
            var Q0;
            Q0=makeQuery(id+"F25.opExtrude","CAP_FACE",FACE,{"disambiguationData":[OSD([sQuery(id+"F24.wireOp",EDGE,"E105")])],"isStart":false});
            extrude(context, id + "F26", {"entities" : qUnion([Q0]), "operationType" : NewBodyOperationType.REMOVE, "oppositeDirection" : true, "depth" : 25.4 * mm, "offsetDistance" : 25.4 * mm});
        }
        {
            var Q0;
            Q0=makeQuery(id+"F25.opExtrude","CAP_EDGE",EDGE,{"disambiguationData":[OSD([sQuery(id+"F24.wireOp",EDGE,"E107")])],"isStart":false});
            var Q1;
            Q1=makeQuery(id+"F25.opExtrude","CAP_EDGE",EDGE,{"disambiguationData":[OSD([sQuery(id+"F24.wireOp",EDGE,"E106")])],"isStart":false});
            var Q2;
            Q2=makeQuery(id+"F26.boolean.opBoolean","COPY",FACE,{"derivedFrom":makeQuery(id+"F26.opExtrude","CAP_FACE",FACE,{"disambiguationData":[OSD([sQuery(id+"F24.wireOp",EDGE,"E105")])],"isStart":false})});
            var Q3;
            Q3=makeQuery(id+"F25.opExtrude","CAP_EDGE",EDGE,{"disambiguationData":[OSD([sQuery(id+"F24.wireOp",EDGE,"E104")])],"isStart":false});
            var Q4;
            Q4=makeQuery(id+"F25.opExtrude","CAP_FACE",FACE,{"disambiguationData":[OSD([sQuery(id+"F24.wireOp",EDGE,"E103")])],"isStart":false});
            fillet(context, id + "F27", {"entities" : qUnion([Q0, Q1, Q2, Q3, Q4]), "radius" : 2.54 * mm, "tangentPropagation" : true, "allowEdgeOverflow" : false});
        }
        {
            var Q0;
            Q0=makeQuery(id+"F8.opExtrude","SWEPT_BODY",BODY,{"disambiguationData":[OSD([sQuery(id+"F5.wireOp",EDGE,"E7"),sQuery(id+"F5.wireOp",EDGE,"E71")])]});
            var Q1;
            Q1=makeQuery(id+"F7.opExtrude","SWEPT_BODY",BODY,{"disambiguationData":[OSD([sQuery(id+"F5.wireOp",EDGE,"E78")])]});
            var Q2;
            Q2=makeQuery(id+"F6.opExtrude","SWEPT_BODY",BODY,{"disambiguationData":[OSD([sQuery(id+"F5.wireOp",EDGE,"E71"),sQuery(id+"F5.wireOp",EDGE,"E72"),sQuery(id+"F5.wireOp",EDGE,"E73"),sQuery(id+"F5.wireOp",EDGE,"E74"),sQuery(id+"F5.wireOp",EDGE,"E77"),sQuery(id+"F5.wireOp",EDGE,"E78")])]});
            var Q3;
            Q3=makeQuery(id+"F7.opExtrude","SWEPT_BODY",BODY,{"disambiguationData":[OSD([sQuery(id+"F5.wireOp",EDGE,"E71"),sQuery(id+"F5.wireOp",EDGE,"E74"),sQuery(id+"F5.wireOp",EDGE,"E75"),sQuery(id+"F5.wireOp",EDGE,"E76"),sQuery(id+"F5.wireOp",EDGE,"E77")])]});
            var Q4;
            Q4=makeQuery(id+"F1.opRevolve","SWEPT_BODY",BODY,{"disambiguationData":[OSD([sQuery(id+"F0.wireOp",EDGE,"E0"),sQuery(id+"F0.wireOp",EDGE,"E1"),sQuery(id+"F0.wireOp",EDGE,"E2"),sQuery(id+"F0.wireOp",EDGE,"E3"),sQuery(id+"F0.wireOp",EDGE,"E4"),sQuery(id+"F0.wireOp",EDGE,"E5")])]});
            var Q5;
            Q5=makeQuery(id+"F6.opExtrude","SWEPT_EDGE",EDGE,{"disambiguationData":[OSD([sQuery(id+"F5.wireOp",EDGE,"E72"),sQuery(id+"F5.wireOp",EDGE,"E73")])]});
            transform(context, id + "F28", {"entities" : qUnion([Q0, Q1, Q2, Q3, Q4]), "transformType" : TransformType.ROTATION, "transformAxis" : qUnion([Q5]), "angle" : 25 * degree, "oppositeDirection" : true, "makeCopy" : false});
        }
        {
            var Q0;
            Q0=makeQuery(id+"F7.opExtrude","SWEPT_BODY",BODY,{"disambiguationData":[OSD([sQuery(id+"F5.wireOp",EDGE,"E78")])]});
            var Q1;
            Q1=makeQuery(id+"F8.opExtrude","SWEPT_BODY",BODY,{"disambiguationData":[OSD([sQuery(id+"F5.wireOp",EDGE,"E7"),sQuery(id+"F5.wireOp",EDGE,"E71")])]});
            var Q2;
            Q2=makeQuery(id+"F6.opExtrude","SWEPT_BODY",BODY,{"disambiguationData":[OSD([sQuery(id+"F5.wireOp",EDGE,"E71"),sQuery(id+"F5.wireOp",EDGE,"E72"),sQuery(id+"F5.wireOp",EDGE,"E73"),sQuery(id+"F5.wireOp",EDGE,"E74"),sQuery(id+"F5.wireOp",EDGE,"E77"),sQuery(id+"F5.wireOp",EDGE,"E78")])]});
            var Q3;
            Q3=makeQuery(id+"F7.opExtrude","SWEPT_BODY",BODY,{"disambiguationData":[OSD([sQuery(id+"F5.wireOp",EDGE,"E71"),sQuery(id+"F5.wireOp",EDGE,"E74"),sQuery(id+"F5.wireOp",EDGE,"E75"),sQuery(id+"F5.wireOp",EDGE,"E76"),sQuery(id+"F5.wireOp",EDGE,"E77")])]});
            var Q4;
            Q4=makeQuery(id+"F1.opRevolve","SWEPT_BODY",BODY,{"disambiguationData":[OSD([sQuery(id+"F0.wireOp",EDGE,"E0"),sQuery(id+"F0.wireOp",EDGE,"E1"),sQuery(id+"F0.wireOp",EDGE,"E2"),sQuery(id+"F0.wireOp",EDGE,"E3"),sQuery(id+"F0.wireOp",EDGE,"E4"),sQuery(id+"F0.wireOp",EDGE,"E5")])]});
            transform(context, id + "F29", {"entities" : qUnion([Q0, Q1, Q2, Q3, Q4]), "transformType" : TransformType.TRANSLATION_3D, "dx" : 0 * mm, "dy" : 67.82 * mm, "dz" : -6.6 * mm, "makeCopy" : false});
        }
        {
            var Q0;
            Q0=makeQuery(id+"F6.opExtrude","CAP_EDGE",EDGE,{"disambiguationData":[OSD([sQuery(id+"F5.wireOp",EDGE,"E73")])],"isStart":false});
            var Q1;
            Q1=makeQuery(id+"F6.opExtrude","CAP_EDGE",EDGE,{"disambiguationData":[OSD([sQuery(id+"F5.wireOp",EDGE,"E74")])],"isStart":false});
            var Q2;
            Q2=makeQuery(id+"F6.opExtrude","CAP_EDGE",EDGE,{"disambiguationData":[OSD([sQuery(id+"F5.wireOp",EDGE,"E73")])],"isStart":true});
            var Q3;
            Q3=makeQuery(id+"F6.opExtrude","CAP_EDGE",EDGE,{"disambiguationData":[OSD([sQuery(id+"F5.wireOp",EDGE,"E74")])],"isStart":true});
            var Q4;
            Q4=makeQuery(id+"F7.opExtrude","CAP_EDGE",EDGE,{"disambiguationData":[OSD([sQuery(id+"F5.wireOp",EDGE,"E74")])],"isStart":true});
            var Q5;
            Q5=makeQuery(id+"F7.opExtrude","CAP_EDGE",EDGE,{"disambiguationData":[OSD([sQuery(id+"F5.wireOp",EDGE,"E74")])],"isStart":false});
            fillet(context, id + "F30", {"entities" : qUnion([Q0, Q1, Q2, Q3, Q4, Q5]), "radius" : 5.08 * mm, "tangentPropagation" : true, "allowEdgeOverflow" : false});
        }
        {
            var Q0;
            Q0=sQuery(id+"F5.wireOp",EDGE,"E99.0");
            var Q1;
            Q1=sQuery(id+"F5.wireOp",VERTEX,"E99.0.start");
            cPlane(context, id + "F31", {"entities" : qUnion([Q0, Q1]), "cplaneType" : CPlaneType.LINE_POINT, "offset" : 25.4 * mm, "width" : 152.4 * mm, "height" : 152.4 * mm});
        }
        {
            var Q0;
            {var subQ3=sQuery(id+"F5.wireOp",EDGE,"E94");Q0=makeQuery(id+"F5.imprint","IMPRINT",FACE,{"disambiguationData":[TD([[makeQuery(id+"F5.imprint","IMPRINT",EDGE,{"derivedFrom":subQ3}),1.0]])]});}
            var Q1;
            {var subQ3=sQuery(id+"F5.wireOp",EDGE,"E93");Q1=makeQuery(id+"F5.imprint","IMPRINT",FACE,{"disambiguationData":[TD([[makeQuery(id+"F5.imprint","IMPRINT",EDGE,{"derivedFrom":subQ3}),-1.0]])]});}
            extrude(context, id + "F32", {"entities" : qUnion([Q0, Q1]), "operationType" : NewBodyOperationType.ADD, "depth" : 6.35 * mm, "offsetDistance" : 25.4 * mm, "symmetric" : true});
        }
        {
            var Q0;
            Q0=makeQuery(id+"F32.opExtrude","CAP_EDGE",EDGE,{"disambiguationData":[OSD([sQuery(id+"F5.wireOp",EDGE,"E93")])],"isStart":false});
            var Q1;
            Q1=makeQuery(id+"F32.opExtrude","CAP_EDGE",EDGE,{"disambiguationData":[OSD([sQuery(id+"F5.wireOp",EDGE,"E98")])],"isStart":false});
            var Q2;
            Q2=makeQuery(id+"F32.opExtrude","CAP_EDGE",EDGE,{"disambiguationData":[OSD([sQuery(id+"F5.wireOp",EDGE,"E95")])],"isStart":false});
            var Q3;
            Q3=makeQuery(id+"F32.opExtrude","CAP_EDGE",EDGE,{"disambiguationData":[OSD([sQuery(id+"F5.wireOp",EDGE,"E94")])],"isStart":false});
            var Q4;
            Q4=makeQuery(id+"F32.opExtrude","CAP_EDGE",EDGE,{"disambiguationData":[OSD([sQuery(id+"F5.wireOp",EDGE,"E95")])],"isStart":true});
            var Q5;
            Q5=makeQuery(id+"F32.opExtrude","CAP_EDGE",EDGE,{"disambiguationData":[OSD([sQuery(id+"F5.wireOp",EDGE,"E94")])],"isStart":true});
            var Q6;
            Q6=makeQuery(id+"F32.opExtrude","CAP_EDGE",EDGE,{"disambiguationData":[OSD([sQuery(id+"F5.wireOp",EDGE,"E97")])],"isStart":true});
            var Q7;
            Q7=makeQuery(id+"F32.opExtrude","CAP_EDGE",EDGE,{"disambiguationData":[OSD([sQuery(id+"F5.wireOp",EDGE,"E98")])],"isStart":true});
            var Q8;
            Q8=makeQuery(id+"F32.opExtrude","CAP_EDGE",EDGE,{"disambiguationData":[OSD([sQuery(id+"F5.wireOp",EDGE,"E93")])],"isStart":true});
            fillet(context, id + "F33", {"entities" : qUnion([Q0, Q1, Q2, Q3, Q4, Q5, Q6, Q7, Q8]), "radius" : 2.54 * mm, "tangentPropagation" : true, "allowEdgeOverflow" : false});
        }
        {
            var Q0;
            Q0=qCreatedBy(makeId("Right.planeOp"),FACE);
            var sketch = newSketch(context, id + "F34", { "sketchPlane" : qUnion([Q0])});
            skLineSegment(sketch, "E108", {"start": v(-55.47, 185.94) * mm, "end": v(-55.43, 189.88) * mm});
            skLineSegment(sketch, "E109", {"start": v(-55.43, 189.88) * mm, "end": v(-45.41, 211.23) * mm});
            skLineSegment(sketch, "E110", {"start": v(-45.41, 211.23) * mm, "end": v(283.34, 207.5) * mm});
            skLineSegment(sketch, "E111", {"start": v(-55.47, 185.94) * mm, "end": v(283.34, 182.1) * mm});
            skLineSegment(sketch, "E112.bottom", {"start": v(-33.3, 186.6) * mm, "end": v(61.94, 185.52) * mm, "construction": true});
            skLineSegment(sketch, "E112.top", {"start": v(-33.05, 209.46) * mm, "end": v(62.2, 208.38) * mm, "construction": true});
            skLineSegment(sketch, "E112.left", {"start": v(-33.3, 186.6) * mm, "end": v(-33.05, 209.46) * mm, "construction": true});
            skLineSegment(sketch, "E112.right", {"start": v(61.94, 185.52) * mm, "end": v(62.2, 208.38) * mm, "construction": true});
            skArc(sketch, "E113", {"start": v(61.94, 185.52) * mm, "mid": v(73.5, 196.82) * mm, "end": v(62.2, 208.38) * mm, "construction": true});
            skLineSegment(sketch, "E114", {"start": v(71.64, 203.19) * mm, "end": v(71.5, 190.5) * mm, "construction": true});
            skLineSegment(sketch, "E115.bottom", {"start": v(166.88, 202.11) * mm, "end": v(71.64, 203.19) * mm, "construction": true});
            skLineSegment(sketch, "E115.top", {"start": v(166.75, 190.13) * mm, "end": v(71.5, 191.21) * mm, "construction": true});
            skLineSegment(sketch, "E115.left", {"start": v(166.88, 202.11) * mm, "end": v(166.75, 190.13) * mm, "construction": true});
            skLineSegment(sketch, "E115.right", {"start": v(71.64, 203.19) * mm, "end": v(71.5, 191.21) * mm, "construction": true});
            skPoint(sketch, "E115.middle", {"position": v(119.2, 196.66) * mm});
            skLineSegment(sketch, "E116", {"start": v(166.88, 205.9) * mm, "end": v(281.18, 204.61) * mm, "construction": true});
            skLineSegment(sketch, "E117", {"start": v(281.18, 204.61) * mm, "end": v(281.18, 185.04) * mm, "construction": true});
            skLineSegment(sketch, "E118", {"start": v(281.18, 185.04) * mm, "end": v(166.88, 186.33) * mm, "construction": true});
            skLineSegment(sketch, "E119", {"start": v(166.88, 186.33) * mm, "end": v(166.88, 205.9) * mm, "construction": true});
            skLineSegment(sketch, "E120", {"start": v(281.18, 194.83) * mm, "end": v(287.53, 194.75) * mm, "construction": true});
            skLineSegment(sketch, "E121", {"start": v(166.82, 196.12) * mm, "end": v(281.18, 194.83) * mm, "construction": true});
            skLineSegment(sketch, "E122", {"start": v(166.88, 202.11) * mm, "end": v(182.44, 201.93) * mm, "construction": true});
            skLineSegment(sketch, "E123", {"start": v(182.44, 201.93) * mm, "end": v(182.3, 189.96) * mm, "construction": true});
            skLineSegment(sketch, "E124", {"start": v(182.3, 189.96) * mm, "end": v(166.75, 190.13) * mm, "construction": true});
            skLineSegment(sketch, "E125", {"start": v(182.44, 201.93) * mm, "end": v(182.47, 204.86) * mm, "construction": true});
            skLineSegment(sketch, "E126", {"start": v(182.47, 204.86) * mm, "end": v(186.5, 204.81) * mm, "construction": true});
            skLineSegment(sketch, "E127", {"start": v(186.5, 204.81) * mm, "end": v(186.3, 186.99) * mm, "construction": true});
            skLineSegment(sketch, "E128", {"start": v(186.3, 186.99) * mm, "end": v(182.27, 187.03) * mm, "construction": true});
            skLineSegment(sketch, "E129", {"start": v(182.27, 187.03) * mm, "end": v(182.3, 189.96) * mm, "construction": true});
            skLineSegment(sketch, "E130", {"start": v(78.67, 207.23) * mm, "end": v(78.44, 187) * mm, "construction": true});
            skLineSegment(sketch, "E131", {"start": v(78.44, 187) * mm, "end": v(82.22, 186.97) * mm});
            skLineSegment(sketch, "E132", {"start": v(82.22, 186.97) * mm, "end": v(82.45, 207.2) * mm, "construction": true});
            skLineSegment(sketch, "E133", {"start": v(82.45, 207.2) * mm, "end": v(78.67, 207.23) * mm, "construction": true});
            skLineSegment(sketch, "E134", {"start": v(82.34, 197.08) * mm, "end": v(166.82, 196.12) * mm, "construction": true});
            skLineSegment(sketch, "E135", {"start": v(283.34, 182.1) * mm, "end": v(290.96, 207.42) * mm});
            skLineSegment(sketch, "E136", {"start": v(265.94, 139.95) * mm, "end": v(282.48, 104.48) * mm});
            skArc(sketch, "E137", {"start": v(130.59, 183.83) * mm, "mid": v(131.69, 166.68) * mm, "end": v(135.35, 149.88) * mm, "construction": true});
            skLineSegment(sketch, "E138", {"start": v(135.35, 149.88) * mm, "end": v(153.93, 87.72) * mm});
            skLineSegment(sketch, "E139", {"start": v(153.93, 87.72) * mm, "end": v(265.94, 139.95) * mm});
            skLineSegment(sketch, "E140", {"start": v(162.25, 170.77) * mm, "end": v(179.34, 113.59) * mm});
            skLineSegment(sketch, "E141", {"start": v(252.04, 169.75) * mm, "end": v(162.25, 170.77) * mm});
            skLineSegment(sketch, "E142", {"start": v(179.34, 113.59) * mm, "end": v(260.57, 151.46) * mm});
            skLineSegment(sketch, "E143", {"start": v(260.57, 151.46) * mm, "end": v(252.04, 169.75) * mm});
            skLineSegment(sketch, "E144", {"start": v(282.48, 104.48) * mm, "end": v(309.92, 117.27) * mm});
            skLineSegment(sketch, "E145", {"start": v(130.59, 183.83) * mm, "end": v(130.64, 188.47) * mm, "construction": true});
            skLineSegment(sketch, "E146", {"start": v(260.57, 151.46) * mm, "end": v(265.94, 139.95) * mm, "construction": true});
            skLineSegment(sketch, "E147", {"start": v(162.25, 170.77) * mm, "end": v(162.4, 183.47) * mm, "construction": true});
            skLineSegment(sketch, "E148", {"start": v(283.34, 207.5) * mm, "end": v(290.96, 207.42) * mm});
            skLineSegment(sketch, "E149", {"start": v(290.96, 207.42) * mm, "end": v(308.14, 207.22) * mm});
            skArc(sketch, "E150", {"start": v(308.14, 207.22) * mm, "mid": v(304.24, 162.15) * mm, "end": v(309.92, 117.27) * mm});
            skLineSegment(sketch, "E151", {"start": v(135.35, 149.88) * mm, "end": v(125.19, 183.9) * mm, "construction": true});
            skLineSegment(sketch, "E152", {"start": v(129, 171.15) * mm, "end": v(119.55, 171.26) * mm});
            skLineSegment(sketch, "E153", {"start": v(119.55, 171.26) * mm, "end": v(115.74, 184) * mm});
            skLineSegment(sketch, "E154", {"start": v(129, 171.15) * mm, "end": v(162.25, 170.77) * mm, "construction": true});
            skLineSegment(sketch, "E155", {"start": v(129, 171.15) * mm, "end": v(135.35, 149.88) * mm});
            skSolve(sketch);
        }
        {
            var Q0;
            {var subQ0=sQuery(id+"F34.wireOp",EDGE,"E135");Q0=makeQuery(id+"F34.imprint","IMPRINT",FACE,{"disambiguationData":[TD([[makeQuery(id+"F34.imprint","IMPRINT",EDGE,{"derivedFrom":subQ0}),-1.0]])]});}
            extrude(context, id + "F35", {"entities" : qUnion([Q0]), "depth" : 25.4 * mm, "offsetDistance" : 25.4 * mm, "symmetric" : true});
        }
        {
            var Q0;
            {var subQ1=sQuery(id+"F34.wireOp",EDGE,"E108");Q0=makeQuery(id+"F34.imprint","IMPRINT",FACE,{"disambiguationData":[TD([[makeQuery(id+"F34.imprint","IMPRINT",EDGE,{"derivedFrom":subQ1}),-1.0]])]});}
            extrude(context, id + "F36", {"entities" : qUnion([Q0]), "depth" : 25.4 * mm, "offsetDistance" : 25.4 * mm, "symmetric" : true});
        }
        {
            var Q0;
            Q0=qCreatedBy(makeId("Right.planeOp"),FACE);
            var sketch = newSketch(context, id + "F37", { "sketchPlane" : qUnion([Q0])});
            skLineSegment(sketch, "E156.bottom", {"start": v(63.34, 205.68) * mm, "end": v(-32.48, 206.76) * mm});
            skLineSegment(sketch, "E156.top", {"start": v(63.14, 188) * mm, "end": v(-32.68, 189.1) * mm});
            skLineSegment(sketch, "E156.left", {"start": v(63.34, 205.68) * mm, "end": v(63.14, 188) * mm, "construction": true});
            skLineSegment(sketch, "E156.right", {"start": v(-32.48, 206.76) * mm, "end": v(-32.68, 189.1) * mm});
            skPoint(sketch, "E156.middle", {"position": v(15.33, 197.39) * mm});
            skArc(sketch, "E157", {"start": v(63.14, 188) * mm, "mid": v(72.08, 196.74) * mm, "end": v(63.34, 205.68) * mm});
            skSolve(sketch);
        }
        {
            var Q0;
            Q0 = qSketchRegion(id + "F37", true);
            extrude(context, id + "F38", {"entities" : qUnion([Q0]), "operationType" : NewBodyOperationType.REMOVE, "depth" : 25.4 * mm, "offsetDistance" : 25.4 * mm});
        }
        {
            var Q0;
            Q0=makeQuery(id+"F36.opExtrude","CAP_EDGE",EDGE,{"disambiguationData":[OSD([sQuery(id+"F34.wireOp",EDGE,"E110"),sQuery(id+"F34.wireOp",EDGE,"E148")])],"isStart":false});
            var Q1;
            Q1=makeQuery(id+"F35.opExtrude","CAP_VERTEX",VERTEX,{"disambiguationData":[OSD([sQuery(id+"F34.wireOp",EDGE,"E135"),sQuery(id+"F34.wireOp",EDGE,"E148"),sQuery(id+"F34.wireOp",EDGE,"E149")])],"isStart":false});
            cPlane(context, id + "F39", {"entities" : qUnion([Q0, Q1]), "cplaneType" : CPlaneType.LINE_POINT, "offset" : 25.4 * mm, "width" : 152.4 * mm, "height" : 152.4 * mm});
        }
        {
            var Q0;
            Q0=qCreatedBy(id+"F39.planeOp",FACE);
            var sketch = newSketch(context, id + "F40", { "sketchPlane" : qUnion([Q0])});
            skLineSegment(sketch, "E158", {"start": v(-12.7, 210.7) * mm, "end": v(12.7, 185.3) * mm, "construction": true});
            skLineSegment(sketch, "E159", {"start": v(12.7, 185.3) * mm, "end": v(12.7, 210.7) * mm, "construction": true});
            skLineSegment(sketch, "E160", {"start": v(12.7, 210.7) * mm, "end": v(-12.7, 185.3) * mm, "construction": true});
            skCircle(sketch, "E161", {"center": v(0, 198) * mm, "radius": 11.86 * mm});
            skSolve(sketch);
        }
        {
            var Q0;
            Q0 = qSketchRegion(id + "F40", true);
            extrude(context, id + "F41", {"entities" : qUnion([Q0]), "operationType" : NewBodyOperationType.REMOVE, "oppositeDirection" : true, "depth" : 332.23 * mm, "offsetDistance" : 25.4 * mm});
        }
        {
            var Q0;
            Q0=makeQuery(id+"F35.opExtrude","CAP_EDGE",EDGE,{"disambiguationData":[OSD([sQuery(id+"F34.wireOp",EDGE,"E140")])],"isStart":false});
            var Q1;
            Q1=makeQuery(id+"F35.opExtrude","CAP_EDGE",EDGE,{"disambiguationData":[OSD([sQuery(id+"F34.wireOp",EDGE,"E140")])],"isStart":true});
            var Q2;
            Q2=makeQuery(id+"F35.opExtrude","CAP_EDGE",EDGE,{"disambiguationData":[OSD([sQuery(id+"F34.wireOp",EDGE,"E143")])],"isStart":false});
            var Q3;
            Q3=makeQuery(id+"F35.opExtrude","CAP_EDGE",EDGE,{"disambiguationData":[OSD([sQuery(id+"F34.wireOp",EDGE,"E143")])],"isStart":true});
            fillet(context, id + "F42", {"entities" : qUnion([Q0, Q1, Q2, Q3]), "radius" : 19.05 * mm, "tangentPropagation" : true, "allowEdgeOverflow" : false});
        }
        {
            var Q0;
            Q0=makeQuery(id+"F35.opExtrude","CAP_EDGE",EDGE,{"disambiguationData":[OSD([sQuery(id+"F34.wireOp",EDGE,"E137")])],"isStart":true});
            var Q1;
            Q1=makeQuery(id+"F35.opExtrude","CAP_EDGE",EDGE,{"disambiguationData":[OSD([sQuery(id+"F34.wireOp",EDGE,"E137")])],"isStart":false});
            var Q2;
            Q2=makeQuery(id+"F35.opExtrude","CAP_EDGE",EDGE,{"disambiguationData":[OSD([sQuery(id+"F34.wireOp",EDGE,"E138")])],"isStart":false});
            fillet(context, id + "F43", {"entities" : qUnion([Q0, Q1, Q2]), "radius" : 2.54 * mm, "tangentPropagation" : true, "allowEdgeOverflow" : false});
        }
        {
            var Q0;
            Q0=makeQuery(id+"F35.opExtrude","CAP_EDGE",EDGE,{"disambiguationData":[OSD([sQuery(id+"F34.wireOp",EDGE,"E153")])],"isStart":false});
            var Q1;
            Q1=makeQuery(id+"F35.opExtrude","CAP_EDGE",EDGE,{"disambiguationData":[OSD([sQuery(id+"F34.wireOp",EDGE,"E153")])],"isStart":true});
            fillet(context, id + "F44", {"entities" : qUnion([Q0, Q1]), "radius" : 12.7 * mm, "tangentPropagation" : true, "allowEdgeOverflow" : false});
        }
        {
            var Q0;
            Q0=makeQuery(id+"F36.opExtrude","CAP_EDGE",EDGE,{"disambiguationData":[OSD([sQuery(id+"F34.wireOp",EDGE,"E111")])],"isStart":false});
            var Q1;
            Q1=makeQuery(id+"F36.opExtrude","CAP_EDGE",EDGE,{"disambiguationData":[OSD([sQuery(id+"F34.wireOp",EDGE,"E110"),sQuery(id+"F34.wireOp",EDGE,"E148")])],"isStart":false});
            var Q2;
            Q2=makeQuery(id+"F36.opExtrude","CAP_EDGE",EDGE,{"disambiguationData":[OSD([sQuery(id+"F34.wireOp",EDGE,"E110"),sQuery(id+"F34.wireOp",EDGE,"E148")])],"isStart":true});
            var Q3;
            Q3=makeQuery(id+"F36.opExtrude","CAP_EDGE",EDGE,{"disambiguationData":[OSD([sQuery(id+"F34.wireOp",EDGE,"E111")])],"isStart":true});
            var Q4;
            Q4=makeQuery(id+"F35.opExtrude","CAP_EDGE",EDGE,{"disambiguationData":[OSD([sQuery(id+"F34.wireOp",EDGE,"E149")])],"isStart":true});
            var Q5;
            Q5=makeQuery(id+"F35.opExtrude","CAP_EDGE",EDGE,{"disambiguationData":[OSD([sQuery(id+"F34.wireOp",EDGE,"E149")])],"isStart":false});
            var Q6;
            Q6=makeQuery(id+"F35.opExtrude","CAP_EDGE",EDGE,{"disambiguationData":[OSD([sQuery(id+"F34.wireOp",EDGE,"E144")])],"isStart":false});
            var Q7;
            Q7=makeQuery(id+"F35.opExtrude","CAP_EDGE",EDGE,{"disambiguationData":[OSD([sQuery(id+"F34.wireOp",EDGE,"E144")])],"isStart":true});
            fillet(context, id + "F45", {"entities" : qUnion([Q0, Q1, Q2, Q3, Q4, Q5, Q6, Q7]), "radius" : 5.08 * mm, "tangentPropagation" : true, "allowEdgeOverflow" : false});
        }
        {
            var Q0;
            Q0=makeQuery(id+"F35.opExtrude","CAP_EDGE",EDGE,{"disambiguationData":[OSD([sQuery(id+"F34.wireOp",EDGE,"E150")])],"isStart":false});
            var Q1;
            Q1=makeQuery(id+"F35.opExtrude","CAP_EDGE",EDGE,{"disambiguationData":[OSD([sQuery(id+"F34.wireOp",EDGE,"E150")])],"isStart":true});
            fillet(context, id + "F46", {"entities" : qUnion([Q0, Q1]), "radius" : 5.08 * mm, "tangentPropagation" : true, "allowEdgeOverflow" : false});
        }
        {
            var Q0;
            Q0=makeQuery(id+"F35.opExtrude","CAP_EDGE",EDGE,{"disambiguationData":[OSD([sQuery(id+"F34.wireOp",EDGE,"E139")])],"isStart":false});
            var Q1;
            {var subQ0=sQuery(id+"F34.wireOp",EDGE,"E153");var subQ1=sQuery(id+"F34.wireOp",EDGE,"E139");Q1=makeQuery(id+"F44.opFillet","BLEND_VERTEX",VERTEX,{"blendedFrom":[makeQuery(id+"F35.opExtrude","CAP_EDGE",EDGE,{"disambiguationData":[OSD([subQ0])],"isStart":false}),makeQuery(id+"F35.opExtrude","SWEPT_FACE",FACE,{"disambiguationData":[OSD([subQ1])]}),makeQuery(id+"F35.opExtrude","CAP_FACE",FACE,{"disambiguationData":[OSD([sQuery(id+"F34.wireOp",EDGE,"E111"),sQuery(id+"F34.wireOp",EDGE,"E135"),sQuery(id+"F34.wireOp",EDGE,"E136"),sQuery(id+"F34.wireOp",EDGE,"E138"),subQ1,sQuery(id+"F34.wireOp",EDGE,"E140"),sQuery(id+"F34.wireOp",EDGE,"E141"),sQuery(id+"F34.wireOp",EDGE,"E142"),sQuery(id+"F34.wireOp",EDGE,"E143"),sQuery(id+"F34.wireOp",EDGE,"E144"),sQuery(id+"F34.wireOp",EDGE,"E149"),sQuery(id+"F34.wireOp",EDGE,"E150"),sQuery(id+"F34.wireOp",EDGE,"E152"),subQ0,sQuery(id+"F34.wireOp",EDGE,"E155")])],"isStart":false})],"blendedInto":[makeQuery(id+"F35.opExtrude","SWEPT_FACE",FACE,{"disambiguationData":[OSD([subQ1])]}),makeQuery(id+"F35.opExtrude","CAP_FACE",FACE,{"disambiguationData":[OSD([sQuery(id+"F34.wireOp",EDGE,"E111"),sQuery(id+"F34.wireOp",EDGE,"E135"),sQuery(id+"F34.wireOp",EDGE,"E136"),sQuery(id+"F34.wireOp",EDGE,"E138"),subQ1,sQuery(id+"F34.wireOp",EDGE,"E140"),sQuery(id+"F34.wireOp",EDGE,"E141"),sQuery(id+"F34.wireOp",EDGE,"E142"),sQuery(id+"F34.wireOp",EDGE,"E143"),sQuery(id+"F34.wireOp",EDGE,"E144"),sQuery(id+"F34.wireOp",EDGE,"E149"),sQuery(id+"F34.wireOp",EDGE,"E150"),sQuery(id+"F34.wireOp",EDGE,"E152"),subQ0,sQuery(id+"F34.wireOp",EDGE,"E155")])],"isStart":false})]});}
            cPlane(context, id + "F47", {"entities" : qUnion([Q0, Q1]), "cplaneType" : CPlaneType.LINE_POINT, "offset" : 25.4 * mm, "width" : 152.4 * mm, "height" : 152.4 * mm});
        }
        {
            var Q0;
            Q0=qCreatedBy(id+"F47.planeOp",FACE);
            var sketch = newSketch(context, id + "F48", { "sketchPlane" : qUnion([Q0])});
            skArc(sketch, "E162", {"start": v(12.7, 14.45) * mm, "mid": v(0, 17.85) * mm, "end": v(-12.7, 14.45) * mm});
            skArc(sketch, "E163", {"start": v(-12.7, 14.45) * mm, "mid": v(0, 8.86) * mm, "end": v(12.7, 14.45) * mm});
            skSolve(sketch);
        }
        {
            var Q0;
            Q0=makeQuery(id+"F48.imprint","IMPRINT",FACE,{"disambiguationData":[TD([[makeQuery(id+"F48.imprint","IMPRINT",EDGE,{"derivedFrom":sQuery(id+"F48.wireOp",EDGE,"E162")}),1.0]])]});
            extrude(context, id + "F49", {"entities" : qUnion([Q0]), "operationType" : NewBodyOperationType.REMOVE, "depth" : 238.86 * mm, "offsetDistance" : 25.4 * mm, "symmetric" : true});
        }
        {
            var Q0;
            Q0=makeQuery(id+"F1.opRevolve","SWEPT_BODY",BODY,{"disambiguationData":[OSD([sQuery(id+"F0.wireOp",EDGE,"E0"),sQuery(id+"F0.wireOp",EDGE,"E1"),sQuery(id+"F0.wireOp",EDGE,"E2"),sQuery(id+"F0.wireOp",EDGE,"E3"),sQuery(id+"F0.wireOp",EDGE,"E4"),sQuery(id+"F0.wireOp",EDGE,"E5")])]});
            var Q1;
            Q1=makeQuery(id+"F8.opExtrude","SWEPT_BODY",BODY,{"disambiguationData":[OSD([sQuery(id+"F5.wireOp",EDGE,"E7"),sQuery(id+"F5.wireOp",EDGE,"E71")])]});
            var Q2;
            Q2=makeQuery(id+"F7.opExtrude","SWEPT_BODY",BODY,{"disambiguationData":[OSD([sQuery(id+"F5.wireOp",EDGE,"E78")])]});
            var Q3;
            Q3=makeQuery(id+"F6.opExtrude","SWEPT_BODY",BODY,{"disambiguationData":[OSD([sQuery(id+"F5.wireOp",EDGE,"E71"),sQuery(id+"F5.wireOp",EDGE,"E72"),sQuery(id+"F5.wireOp",EDGE,"E73"),sQuery(id+"F5.wireOp",EDGE,"E74"),sQuery(id+"F5.wireOp",EDGE,"E77"),sQuery(id+"F5.wireOp",EDGE,"E78")])]});
            var Q4;
            Q4=makeQuery(id+"F7.opExtrude","SWEPT_BODY",BODY,{"disambiguationData":[OSD([sQuery(id+"F5.wireOp",EDGE,"E71"),sQuery(id+"F5.wireOp",EDGE,"E74"),sQuery(id+"F5.wireOp",EDGE,"E75"),sQuery(id+"F5.wireOp",EDGE,"E76"),sQuery(id+"F5.wireOp",EDGE,"E77")])]});
            var Q5;
            Q5=makeQuery(id+"F6.opExtrude","SWEPT_EDGE",EDGE,{"disambiguationData":[OSD([sQuery(id+"F5.wireOp",EDGE,"E72"),sQuery(id+"F5.wireOp",EDGE,"E73")])]});
            transform(context, id + "F50", {"entities" : qUnion([Q0, Q1, Q2, Q3, Q4]), "transformType" : TransformType.ROTATION, "transformAxis" : qUnion([Q5]), "angle" : 25 * degree, "makeCopy" : false});
        }
        {
            var Q0;
            Q0=makeQuery(id+"F8.opExtrude","SWEPT_BODY",BODY,{"disambiguationData":[OSD([sQuery(id+"F5.wireOp",EDGE,"E7"),sQuery(id+"F5.wireOp",EDGE,"E71")])]});
            var Q1;
            Q1=makeQuery(id+"F7.opExtrude","SWEPT_BODY",BODY,{"disambiguationData":[OSD([sQuery(id+"F5.wireOp",EDGE,"E78")])]});
            var Q2;
            Q2=makeQuery(id+"F6.opExtrude","SWEPT_BODY",BODY,{"disambiguationData":[OSD([sQuery(id+"F5.wireOp",EDGE,"E71"),sQuery(id+"F5.wireOp",EDGE,"E72"),sQuery(id+"F5.wireOp",EDGE,"E73"),sQuery(id+"F5.wireOp",EDGE,"E74"),sQuery(id+"F5.wireOp",EDGE,"E77"),sQuery(id+"F5.wireOp",EDGE,"E78")])]});
            var Q3;
            Q3=makeQuery(id+"F7.opExtrude","SWEPT_BODY",BODY,{"disambiguationData":[OSD([sQuery(id+"F5.wireOp",EDGE,"E71"),sQuery(id+"F5.wireOp",EDGE,"E74"),sQuery(id+"F5.wireOp",EDGE,"E75"),sQuery(id+"F5.wireOp",EDGE,"E76"),sQuery(id+"F5.wireOp",EDGE,"E77")])]});
            var Q4;
            Q4=makeQuery(id+"F1.opRevolve","SWEPT_BODY",BODY,{"disambiguationData":[OSD([sQuery(id+"F0.wireOp",EDGE,"E0"),sQuery(id+"F0.wireOp",EDGE,"E1"),sQuery(id+"F0.wireOp",EDGE,"E2"),sQuery(id+"F0.wireOp",EDGE,"E3"),sQuery(id+"F0.wireOp",EDGE,"E4"),sQuery(id+"F0.wireOp",EDGE,"E5")])]});
            transform(context, id + "F51", {"entities" : qUnion([Q0, Q1, Q2, Q3, Q4]), "transformType" : TransformType.TRANSLATION_3D, "dx" : 0 * mm, "dy" : -67.06 * mm, "dz" : 6.6 * mm, "makeCopy" : false});
        }
    });
